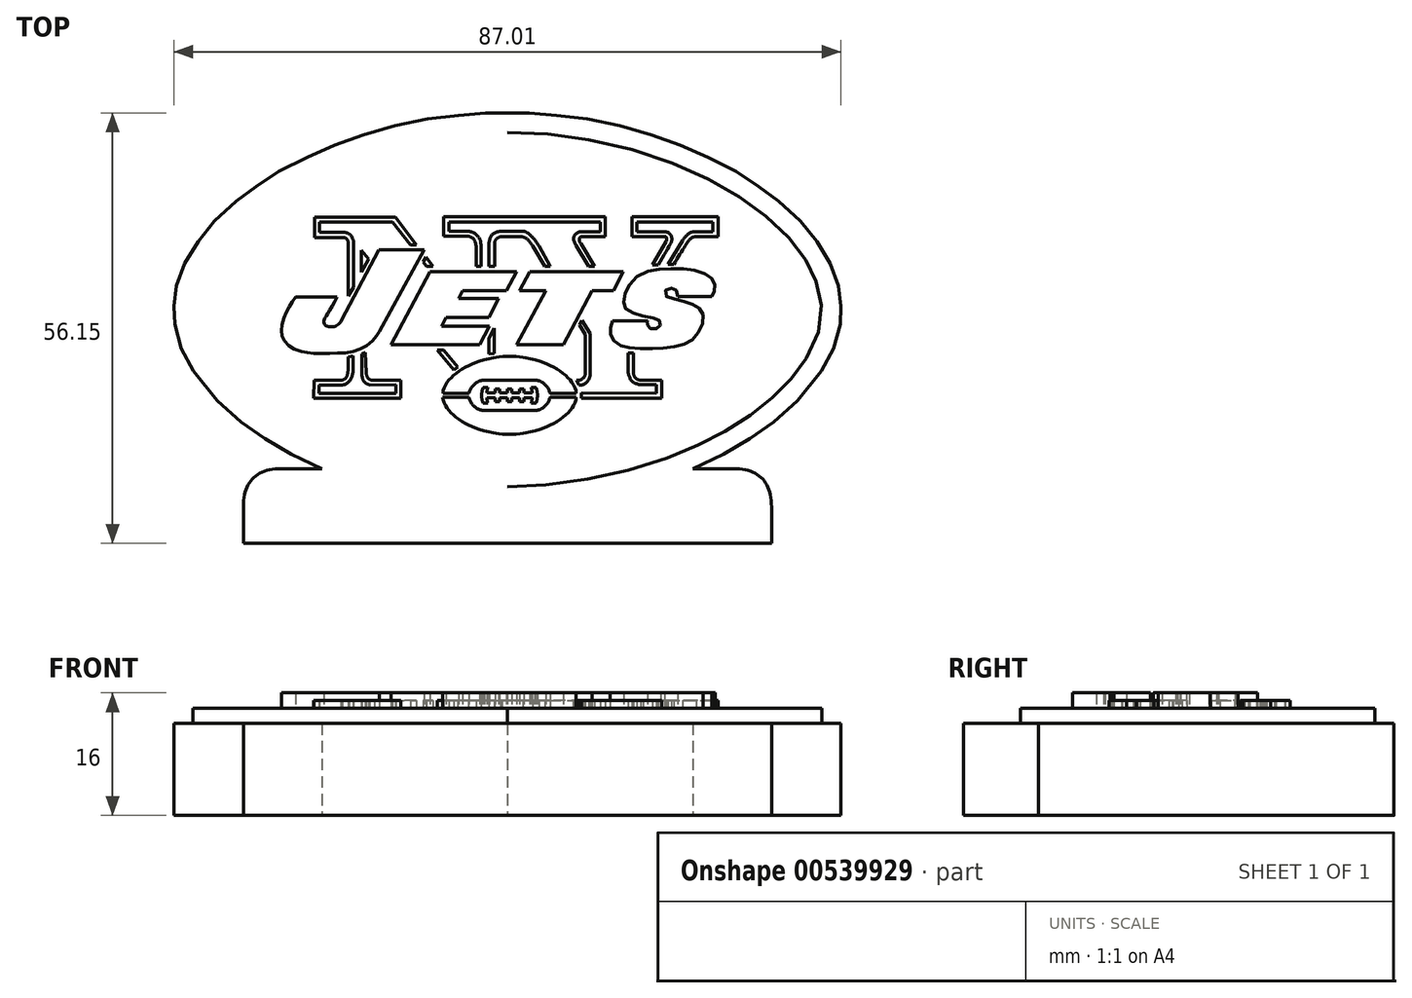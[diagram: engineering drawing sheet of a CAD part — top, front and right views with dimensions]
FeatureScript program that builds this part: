
annotation { "Feature Type Name" : "Feature", "Feature Type Description" : "" }
export const myFeature = defineFeature(function(context is Context, id is Id, definition is map)
    precondition{}
    {
        {
            var Q0;
            Q0=qCreatedBy(makeId("Top.planeOp"),FACE);
            var sketch = newSketch(context, id + "F0", { "sketchPlane" : qUnion([Q0])});
            skLineSegment(sketch, "E0", {"start": v(50, 100) * mm, "end": v(50, 0) * mm, "construction": true});
            skLineSegment(sketch, "E1", {"start": v(0, 50) * mm, "end": v(100, 50) * mm, "construction": true});
            skFitSpline(sketch, "E2", {"points": [v(50, 73.16) * mm, v(46.62, 73.07) * mm, v(44.13, 72.89) * mm, v(41.3, 72.55) * mm, v(37.34, 71.82) * mm, v(34.12, 71.04) * mm, v(31.1, 70.1) * mm, v(27.86, 68.92) * mm, v(25.45, 67.89) * mm, v(22.77, 66.55) * mm, v(20.87, 65.46) * mm, v(18.96, 64.22) * mm, v(17.3, 63.01) * mm, v(15.95, 61.91) * mm, v(14.34, 60.56) * mm, v(13.3, 59.43) * mm, v(12.35, 58.37) * mm, v(11.4, 57.02) * mm, v(10.87, 56.17) * mm, v(10.37, 55.3) * mm, v(9.9, 54.28) * mm, v(9.6, 53.32) * mm, v(9.3, 52.32) * mm, v(9.13, 51.17) * mm, v(9, 50.05) * mm, v(9.13, 48.63) * mm, v(9.42, 47.24) * mm, v(9.9, 45.89) * mm, v(10.55, 44.44) * mm, v(11.33, 43.21) * mm, v(12.02, 42.28) * mm, v(12.76, 41.3) * mm, v(13.44, 40.51) * mm, v(14.34, 39.6) * mm, v(15.47, 38.57) * mm, v(16.53, 37.65) * mm, v(17.63, 36.8) * mm, v(18.94, 35.88) * mm, v(20.3, 34.98) * mm, v(21.76, 34.1) * mm, v(23.17, 33.3) * mm, v(24.65, 32.6) * mm, v(26.26, 31.88) * mm, v(28.27, 31.03) * mm, v(30.62, 30.16) * mm, v(33.75, 29.24) * mm, v(36.82, 28.44) * mm, v(39.85, 27.86) * mm, v(43.18, 27.36) * mm, v(46.75, 27.08) * mm, v(49.83, 26.94) * mm, v(50, 26.94) * mm], "startDerivative": vector(-134.06, -2.29) * mm, "endDerivative": vector(19.01, 1.2) * mm});
            skFitSpline(sketch, "E3.MirrorCS", {"points": [v(50, 73.16) * mm, v(53.38, 73.07) * mm, v(55.87, 72.89) * mm, v(58.7, 72.55) * mm, v(62.66, 71.82) * mm, v(65.88, 71.04) * mm, v(68.9, 70.1) * mm, v(72.14, 68.92) * mm, v(74.55, 67.89) * mm, v(77.23, 66.55) * mm, v(79.13, 65.46) * mm, v(81.04, 64.22) * mm, v(82.7, 63.01) * mm, v(84.05, 61.91) * mm, v(85.66, 60.56) * mm, v(86.7, 59.43) * mm, v(87.65, 58.37) * mm, v(88.6, 57.02) * mm, v(89.13, 56.17) * mm, v(89.63, 55.3) * mm, v(90.1, 54.28) * mm, v(90.4, 53.32) * mm, v(90.7, 52.32) * mm, v(90.87, 51.17) * mm, v(91, 50.05) * mm, v(90.87, 48.63) * mm, v(90.58, 47.24) * mm, v(90.1, 45.89) * mm, v(89.45, 44.44) * mm, v(88.67, 43.21) * mm, v(87.98, 42.28) * mm, v(87.24, 41.3) * mm, v(86.56, 40.51) * mm, v(85.66, 39.6) * mm, v(84.53, 38.57) * mm, v(83.47, 37.65) * mm, v(82.37, 36.8) * mm, v(81.06, 35.88) * mm, v(79.7, 34.98) * mm, v(78.24, 34.1) * mm, v(76.83, 33.3) * mm, v(75.35, 32.6) * mm, v(73.74, 31.88) * mm, v(71.73, 31.03) * mm, v(69.38, 30.16) * mm, v(66.25, 29.24) * mm, v(63.18, 28.44) * mm, v(60.15, 27.86) * mm, v(56.82, 27.36) * mm, v(53.25, 27.08) * mm, v(50.17, 26.94) * mm, v(50, 26.94) * mm], "startDerivative": vector(134.06, -2.29) * mm, "endDerivative": vector(-19.01, 1.2) * mm});
            skSolve(sketch);
        }
        {
            var Q0;
            Q0=qCreatedBy(makeId("Top.planeOp"),FACE);
            var sketch = newSketch(context, id + "F1", { "sketchPlane" : qUnion([Q0])});
            skLineSegment(sketch, "E4", {"start": v(50, 100) * mm, "end": v(50, 2.23) * mm, "construction": true});
            skFitSpline(sketch, "E5", {"points": [v(50, 75.68) * mm, v(48.22, 75.7) * mm, v(45.68, 75.58) * mm, v(42.43, 75.28) * mm, v(38.32, 74.7) * mm, v(33.84, 73.64) * mm, v(29.88, 72.39) * mm, v(26.53, 71.15) * mm, v(23.08, 69.55) * mm, v(19.5, 67.67) * mm, v(17.21, 66.1) * mm, v(15.36, 64.76) * mm, v(12.75, 62.51) * mm, v(10.58, 60.22) * mm, v(9.15, 58.19) * mm, v(7.8, 55.82) * mm, v(6.96, 53.56) * mm, v(6.6, 52.08) * mm, v(6.5, 50.12) * mm, v(6.52, 48.8) * mm, v(6.73, 47.54) * mm, v(7.56, 44.73) * mm, v(8.64, 42.63) * mm, v(12.08, 38.23) * mm, v(15.22, 35.44) * mm, v(18, 33.43) * mm, v(21.12, 31.58) * mm, v(25.16, 29.58) * mm, v(30.48, 27.6) * mm, v(35.66, 26.1) * mm, v(39.54, 25.32) * mm, v(45.3, 24.56) * mm, v(47.72, 24.4) * mm, v(50, 24.42) * mm], "startDerivative": vector(-75.7, 2.02) * mm, "endDerivative": vector(91.69, 1.96) * mm});
            skFitSpline(sketch, "E6.MirrorCS", {"points": [v(50, 75.68) * mm, v(51.79, 75.7) * mm, v(54.32, 75.58) * mm, v(57.57, 75.28) * mm, v(61.69, 74.7) * mm, v(66.17, 73.64) * mm, v(70.13, 72.39) * mm, v(73.48, 71.15) * mm, v(76.93, 69.55) * mm, v(80.5, 67.67) * mm, v(82.8, 66.1) * mm, v(84.65, 64.76) * mm, v(87.25, 62.51) * mm, v(89.42, 60.22) * mm, v(90.86, 58.19) * mm, v(92.21, 55.82) * mm, v(93.04, 53.56) * mm, v(93.4, 52.08) * mm, v(93.5, 50.12) * mm, v(93.49, 48.8) * mm, v(93.28, 47.54) * mm, v(92.45, 44.73) * mm, v(91.37, 42.63) * mm, v(87.93, 38.23) * mm, v(84.78, 35.44) * mm, v(82, 33.43) * mm, v(78.89, 31.58) * mm, v(74.85, 29.58) * mm, v(69.53, 27.6) * mm, v(64.35, 26.1) * mm, v(60.47, 25.32) * mm, v(54.7, 24.56) * mm, v(52.28, 24.4) * mm, v(50, 24.42) * mm], "startDerivative": vector(75.7, 2.02) * mm, "endDerivative": vector(-91.69, 1.96) * mm});
            skLineSegment(sketch, "E7.bottom", {"start": v(84.45, 19.55) * mm, "end": v(15.56, 19.55) * mm});
            skLineSegment(sketch, "E7.top", {"start": v(84.45, 29.3) * mm, "end": v(15.56, 29.3) * mm});
            skLineSegment(sketch, "E7.left", {"start": v(84.45, 19.55) * mm, "end": v(84.45, 29.3) * mm});
            skLineSegment(sketch, "E7.right", {"start": v(15.56, 19.55) * mm, "end": v(15.56, 29.3) * mm});
            skSolve(sketch);
        }
        {
            var Q0;
            Q0 = qSketchRegion(id + "F1", true);
            extrude(context, id + "F2", {"entities" : qUnion([Q0]), "depth" : 12 * mm, "offsetDistance" : 25.4 * mm});
        }
        {
            var Q0;
            Q0 = qSketchRegion(id + "F0", true);
            extrude(context, id + "F3", {"entities" : qUnion([Q0]), "operationType" : NewBodyOperationType.ADD, "depth" : 14 * mm, "offsetDistance" : 25.4 * mm});
        }
        {
            var Q0;
            Q0=qCreatedBy(makeId("Top.planeOp"),FACE);
            var sketch = newSketch(context, id + "F4", { "sketchPlane" : qUnion([Q0])});
            skLineSegment(sketch, "E8", {"start": v(24.85, 62.05) * mm, "end": v(24.85, 59.47) * mm});
            skLineSegment(sketch, "E9", {"start": v(24.85, 59.47) * mm, "end": v(28.43, 59.47) * mm});
            skFitSpline(sketch, "E10", {"points": [v(28.43, 59.47) * mm, v(28.84, 59.42) * mm, v(29.08, 59.22) * mm, v(29.18, 59.04) * mm, v(29.23, 58.86) * mm, v(29.25, 58.52) * mm], "startDerivative": vector(1.8, 0.01) * mm, "endDerivative": vector(0.05, -1.65) * mm});
            skLineSegment(sketch, "E11", {"start": v(29.25, 58.52) * mm, "end": v(29.25, 51.84) * mm});
            skLineSegment(sketch, "E12", {"start": v(29.25, 51.84) * mm, "end": v(29.95, 52.98) * mm});
            skLineSegment(sketch, "E13", {"start": v(29.95, 52.98) * mm, "end": v(29.95, 58.77) * mm});
            skFitSpline(sketch, "E14", {"points": [v(29.95, 58.77) * mm, v(29.82, 59.32) * mm, v(29.41, 59.87) * mm, v(28.81, 60.12) * mm, v(28.46, 60.15) * mm], "startDerivative": vector(-0.34, 2.18) * mm, "endDerivative": vector(-1.62, -0.01) * mm});
            skLineSegment(sketch, "E15", {"start": v(28.46, 60.15) * mm, "end": v(25.49, 60.15) * mm});
            skLineSegment(sketch, "E16", {"start": v(25.49, 60.15) * mm, "end": v(25.49, 61.46) * mm});
            skLineSegment(sketch, "E17", {"start": v(25.49, 61.46) * mm, "end": v(35.03, 61.46) * mm});
            skLineSegment(sketch, "E18", {"start": v(35.03, 61.46) * mm, "end": v(37.34, 58.48) * mm});
            skLineSegment(sketch, "E19", {"start": v(37.34, 58.48) * mm, "end": v(38.12, 58.48) * mm});
            skLineSegment(sketch, "E20", {"start": v(38.12, 58.48) * mm, "end": v(35.37, 62.1) * mm});
            skLineSegment(sketch, "E21", {"start": v(35.37, 62.1) * mm, "end": v(24.85, 62.1) * mm});
            skLineSegment(sketch, "E22", {"start": v(24.85, 62.1) * mm, "end": v(24.85, 62.05) * mm});
            skLineSegment(sketch, "E23", {"start": v(30.93, 57.77) * mm, "end": v(30.93, 54.9) * mm});
            skLineSegment(sketch, "E24", {"start": v(30.93, 54.9) * mm, "end": v(31.9, 56.66) * mm});
            skLineSegment(sketch, "E25", {"start": v(31.9, 56.66) * mm, "end": v(30.93, 57.77) * mm});
            skLineSegment(sketch, "E26", {"start": v(39.37, 56.87) * mm, "end": v(40.3, 55.67) * mm});
            skLineSegment(sketch, "E27", {"start": v(40.3, 55.67) * mm, "end": v(39.45, 55.67) * mm});
            skLineSegment(sketch, "E28", {"start": v(39.45, 55.67) * mm, "end": v(39, 56.26) * mm});
            skLineSegment(sketch, "E29", {"start": v(39, 56.26) * mm, "end": v(39.37, 56.87) * mm});
            skLineSegment(sketch, "E30", {"start": v(29.33, 43.9) * mm, "end": v(29.9, 43.98) * mm});
            skLineSegment(sketch, "E31", {"start": v(29.9, 43.98) * mm, "end": v(29.9, 42.3) * mm});
            skFitSpline(sketch, "E32", {"points": [v(29.9, 42.3) * mm, v(29.81, 41.7) * mm, v(29.65, 41.15) * mm, v(29.36, 40.66) * mm, v(28.93, 40.35) * mm, v(28.7, 40.25) * mm, v(28.25, 40.21) * mm], "startDerivative": vector(-0.33, -3.22) * mm, "endDerivative": vector(-3.09, -0.14) * mm});
            skLineSegment(sketch, "E33", {"start": v(28.25, 40.21) * mm, "end": v(25.45, 40.21) * mm});
            skLineSegment(sketch, "E34", {"start": v(25.45, 40.21) * mm, "end": v(25.45, 39.1) * mm});
            skLineSegment(sketch, "E35", {"start": v(25.45, 39.1) * mm, "end": v(35.46, 39.1) * mm});
            skLineSegment(sketch, "E36", {"start": v(35.46, 39.1) * mm, "end": v(35.46, 40.25) * mm});
            skLineSegment(sketch, "E37", {"start": v(35.46, 40.25) * mm, "end": v(32.05, 40.21) * mm});
            skFitSpline(sketch, "E38", {"points": [v(32.05, 40.21) * mm, v(31.62, 40.38) * mm, v(31.27, 40.68) * mm, v(31.08, 41.12) * mm, v(30.98, 41.8) * mm], "startDerivative": vector(-1.88, 0.6) * mm, "endDerivative": vector(-0.28, 2.5) * mm});
            skLineSegment(sketch, "E39", {"start": v(30.98, 41.8) * mm, "end": v(30.98, 44.23) * mm});
            skLineSegment(sketch, "E40", {"start": v(30.98, 44.23) * mm, "end": v(31.47, 44.47) * mm});
            skLineSegment(sketch, "E41", {"start": v(31.47, 44.47) * mm, "end": v(31.56, 41.8) * mm});
            skFitSpline(sketch, "E42", {"points": [v(31.56, 41.8) * mm, v(31.64, 41.47) * mm, v(31.78, 41.15) * mm, v(32.09, 40.9) * mm, v(32.69, 40.84) * mm], "startDerivative": vector(0.33, -1.48) * mm, "endDerivative": vector(2.17, 0.04) * mm});
            skLineSegment(sketch, "E43", {"start": v(32.69, 40.84) * mm, "end": v(36.1, 40.84) * mm});
            skLineSegment(sketch, "E44", {"start": v(36.1, 40.84) * mm, "end": v(36.1, 38.49) * mm});
            skLineSegment(sketch, "E45", {"start": v(36.1, 38.49) * mm, "end": v(24.72, 38.49) * mm});
            skLineSegment(sketch, "E46", {"start": v(24.72, 38.49) * mm, "end": v(24.78, 40.84) * mm});
            skLineSegment(sketch, "E47", {"start": v(24.78, 40.84) * mm, "end": v(28.44, 40.84) * mm});
            skFitSpline(sketch, "E48", {"points": [v(28.44, 40.84) * mm, v(28.7, 40.94) * mm, v(28.98, 41.21) * mm, v(29.15, 41.67) * mm, v(29.23, 42.24) * mm], "startDerivative": vector(1.26, 0.37) * mm, "endDerivative": vector(0.2, 1.98) * mm});
            skLineSegment(sketch, "E49", {"start": v(29.23, 42.24) * mm, "end": v(29.23, 43.86) * mm});
            skLineSegment(sketch, "E50", {"start": v(29.23, 43.86) * mm, "end": v(29.33, 43.9) * mm});
            skLineSegment(sketch, "E51", {"start": v(40.87, 44.77) * mm, "end": v(41.67, 44.77) * mm});
            skLineSegment(sketch, "E52", {"start": v(41.67, 44.77) * mm, "end": v(43.5, 42.57) * mm});
            skLineSegment(sketch, "E53", {"start": v(43.5, 42.57) * mm, "end": v(43, 42.14) * mm});
            skLineSegment(sketch, "E54", {"start": v(43, 42.14) * mm, "end": v(40.87, 44.77) * mm});
            skLineSegment(sketch, "E55", {"start": v(48.29, 47.62) * mm, "end": v(48.29, 44.32) * mm});
            skLineSegment(sketch, "E56", {"start": v(48.29, 44.32) * mm, "end": v(47.56, 44.23) * mm});
            skLineSegment(sketch, "E57", {"start": v(47.56, 44.23) * mm, "end": v(47.56, 46.32) * mm});
            skLineSegment(sketch, "E58", {"start": v(47.56, 46.32) * mm, "end": v(48.29, 47.62) * mm});
            skLineSegment(sketch, "E59", {"start": v(41.76, 62.14) * mm, "end": v(62.77, 62.14) * mm});
            skLineSegment(sketch, "E60", {"start": v(62.77, 62.14) * mm, "end": v(62.77, 59.58) * mm});
            skLineSegment(sketch, "E61", {"start": v(62.77, 59.58) * mm, "end": v(59.8, 59.58) * mm});
            skFitSpline(sketch, "E62", {"points": [v(59.8, 59.58) * mm, v(59.61, 59.58) * mm, v(59.4, 59.4) * mm, v(59.39, 59.1) * mm, v(59.45, 58.85) * mm, v(59.57, 58.66) * mm], "startDerivative": vector(-1.04, 0.18) * mm, "endDerivative": vector(0.66, -0.95) * mm});
            skLineSegment(sketch, "E63", {"start": v(59.57, 58.66) * mm, "end": v(61.39, 55.71) * mm});
            skLineSegment(sketch, "E64", {"start": v(61.39, 55.71) * mm, "end": v(60.62, 55.71) * mm});
            skLineSegment(sketch, "E65", {"start": v(60.62, 55.71) * mm, "end": v(58.93, 58.43) * mm});
            skFitSpline(sketch, "E66", {"points": [v(58.93, 58.43) * mm, v(58.73, 58.9) * mm, v(58.63, 59.3) * mm, v(58.73, 59.7) * mm, v(58.93, 59.92) * mm, v(59.34, 60.15) * mm, v(59.95, 60.2) * mm], "startDerivative": vector(-1.2, 2.65) * mm, "endDerivative": vector(3.3, -0.07) * mm});
            skLineSegment(sketch, "E67", {"start": v(59.95, 60.2) * mm, "end": v(62.15, 60.2) * mm});
            skLineSegment(sketch, "E68", {"start": v(62.15, 60.2) * mm, "end": v(62.15, 61.5) * mm});
            skLineSegment(sketch, "E69", {"start": v(62.15, 61.5) * mm, "end": v(42.37, 61.5) * mm});
            skLineSegment(sketch, "E70", {"start": v(42.37, 61.5) * mm, "end": v(42.37, 60.25) * mm});
            skLineSegment(sketch, "E71", {"start": v(42.37, 60.25) * mm, "end": v(44.9, 60.25) * mm});
            skFitSpline(sketch, "E72", {"points": [v(44.9, 60.25) * mm, v(45.38, 60.15) * mm, v(45.82, 59.93) * mm, v(46.2, 59.53) * mm, v(46.4, 59.18) * mm, v(46.53, 58.67) * mm, v(46.57, 58.2) * mm], "startDerivative": vector(2.94, -0.53) * mm, "endDerivative": vector(0.11, -2.77) * mm});
            skLineSegment(sketch, "E73", {"start": v(46.57, 58.2) * mm, "end": v(46.57, 55.66) * mm});
            skLineSegment(sketch, "E74", {"start": v(46.57, 55.66) * mm, "end": v(45.98, 55.66) * mm});
            skLineSegment(sketch, "E75", {"start": v(45.98, 55.66) * mm, "end": v(45.93, 55.66) * mm});
            skLineSegment(sketch, "E76", {"start": v(45.93, 55.66) * mm, "end": v(45.93, 58.24) * mm});
            skFitSpline(sketch, "E77", {"points": [v(45.93, 58.24) * mm, v(45.8, 58.84) * mm, v(45.6, 59.24) * mm, v(45.31, 59.48) * mm, v(45.04, 59.6) * mm, v(44.52, 59.62) * mm], "startDerivative": vector(-0.4, 2.67) * mm, "endDerivative": vector(-2.63, -0.01) * mm});
            skLineSegment(sketch, "E78", {"start": v(44.52, 59.62) * mm, "end": v(41.7, 59.62) * mm});
            skLineSegment(sketch, "E79", {"start": v(41.7, 59.62) * mm, "end": v(41.7, 62.14) * mm});
            skLineSegment(sketch, "E80", {"start": v(41.7, 62.14) * mm, "end": v(41.76, 62.14) * mm});
            skLineSegment(sketch, "E81", {"start": v(47.57, 55.66) * mm, "end": v(48.35, 55.66) * mm});
            skLineSegment(sketch, "E82", {"start": v(48.35, 55.66) * mm, "end": v(48.35, 58.5) * mm});
            skLineSegment(sketch, "E83", {"start": v(47.57, 55.66) * mm, "end": v(47.57, 58.55) * mm});
            skFitSpline(sketch, "E84", {"points": [v(47.57, 58.55) * mm, v(47.68, 59.14) * mm, v(47.86, 59.65) * mm, v(48.32, 60.05) * mm, v(48.76, 60.2) * mm, v(49.07, 60.27) * mm, v(49.27, 60.28) * mm], "startDerivative": vector(0.55, 3.05) * mm, "endDerivative": vector(1.75, -0.03) * mm});
            skLineSegment(sketch, "E85", {"start": v(49.27, 60.28) * mm, "end": v(52.02, 60.28) * mm});
            skFitSpline(sketch, "E86", {"points": [v(52.02, 60.28) * mm, v(52.4, 60.17) * mm, v(52.82, 59.91) * mm, v(53.21, 59.55) * mm, v(53.62, 59.08) * mm, v(54.1, 58.36) * mm], "startDerivative": vector(2.3, -0.47) * mm, "endDerivative": vector(1.98, -3.12) * mm});
            skLineSegment(sketch, "E87", {"start": v(54.1, 58.36) * mm, "end": v(55.6, 55.67) * mm});
            skLineSegment(sketch, "E88", {"start": v(55.6, 55.67) * mm, "end": v(54.87, 55.67) * mm});
            skLineSegment(sketch, "E89", {"start": v(54.87, 55.67) * mm, "end": v(53.32, 58.36) * mm});
            skFitSpline(sketch, "E90", {"points": [v(53.32, 58.36) * mm, v(53.06, 58.7) * mm, v(52.77, 59.05) * mm, v(52.37, 59.39) * mm, v(52.1, 59.5) * mm, v(51.86, 59.57) * mm, v(51.4, 59.59) * mm], "startDerivative": vector(-1.5, 2) * mm, "endDerivative": vector(-2.75, 0) * mm});
            skLineSegment(sketch, "E91", {"start": v(51.4, 59.59) * mm, "end": v(49.1, 59.57) * mm});
            skFitSpline(sketch, "E92", {"points": [v(48.35, 58.5) * mm, v(48.35, 58.68) * mm, v(48.4, 59.03) * mm, v(48.53, 59.22) * mm, v(48.79, 59.44) * mm, v(49.1, 59.57) * mm], "startDerivative": vector(-0.02, 1.04) * mm, "endDerivative": vector(1.44, 0.46) * mm});
            skLineSegment(sketch, "E93", {"start": v(66.24, 59.58) * mm, "end": v(66.24, 62.14) * mm});
            skLineSegment(sketch, "E94", {"start": v(66.24, 62.14) * mm, "end": v(77.52, 62.14) * mm});
            skLineSegment(sketch, "E95", {"start": v(77.52, 62.14) * mm, "end": v(77.52, 59.58) * mm});
            skLineSegment(sketch, "E96", {"start": v(77.52, 59.58) * mm, "end": v(74.65, 59.58) * mm});
            skFitSpline(sketch, "E97", {"points": [v(74.65, 59.58) * mm, v(74.36, 59.54) * mm, v(73.99, 59.38) * mm, v(73.63, 59.02) * mm, v(71.69, 55.96) * mm], "startDerivative": vector(-1.91, -0.1) * mm, "endDerivative": vector(-4.67, -7.57) * mm});
            skLineSegment(sketch, "E98", {"start": v(71.69, 55.96) * mm, "end": v(70.96, 55.96) * mm});
            skLineSegment(sketch, "E99", {"start": v(70.96, 55.96) * mm, "end": v(72.84, 59.08) * mm});
            skFitSpline(sketch, "E100", {"points": [v(72.84, 59.08) * mm, v(73.16, 59.5) * mm, v(73.57, 59.88) * mm, v(74, 60.14) * mm, v(74.5, 60.2) * mm, v(75.12, 60.21) * mm], "startDerivative": vector(1.5, 2.2) * mm, "endDerivative": vector(2.99, 0.01) * mm});
            skLineSegment(sketch, "E101", {"start": v(75.12, 60.21) * mm, "end": v(76.81, 60.21) * mm});
            skLineSegment(sketch, "E102", {"start": v(76.81, 60.21) * mm, "end": v(76.81, 61.48) * mm});
            skLineSegment(sketch, "E103", {"start": v(76.81, 61.48) * mm, "end": v(66.86, 61.48) * mm});
            skLineSegment(sketch, "E104", {"start": v(66.86, 61.48) * mm, "end": v(66.86, 60.21) * mm});
            skLineSegment(sketch, "E105", {"start": v(66.86, 60.21) * mm, "end": v(70.6, 60.21) * mm});
            skFitSpline(sketch, "E106", {"points": [v(70.6, 60.21) * mm, v(70.9, 60.14) * mm, v(71.15, 59.96) * mm, v(71.36, 59.65) * mm, v(71.44, 59.35) * mm, v(71.43, 59.05) * mm, v(71.33, 58.76) * mm, v(69.68, 55.87) * mm], "startDerivative": vector(2.92, -0.46) * mm, "endDerivative": vector(-6.14, -10.46) * mm});
            skLineSegment(sketch, "E107", {"start": v(69.68, 55.87) * mm, "end": v(68.9, 55.87) * mm});
            skLineSegment(sketch, "E108", {"start": v(68.9, 55.87) * mm, "end": v(70.7, 58.9) * mm});
            skFitSpline(sketch, "E109", {"points": [v(70.7, 58.9) * mm, v(70.74, 59.07) * mm, v(70.75, 59.34) * mm, v(70.7, 59.52) * mm, v(70.49, 59.58) * mm], "startDerivative": vector(0.2, 0.65) * mm, "endDerivative": vector(-1.01, 0.12) * mm});
            skLineSegment(sketch, "E110", {"start": v(70.49, 59.58) * mm, "end": v(66.24, 59.58) * mm});
            skLineSegment(sketch, "E111", {"start": v(59.73, 48.66) * mm, "end": v(59.38, 48.05) * mm});
            skLineSegment(sketch, "E112", {"start": v(59.38, 48.05) * mm, "end": v(60.15, 46.79) * mm});
            skLineSegment(sketch, "E113", {"start": v(60.15, 46.79) * mm, "end": v(60.15, 41.83) * mm});
            skLineSegment(sketch, "E114", {"start": v(59.73, 48.66) * mm, "end": v(60.82, 46.9) * mm});
            skLineSegment(sketch, "E115", {"start": v(60.82, 46.9) * mm, "end": v(60.82, 41.67) * mm});
            skFitSpline(sketch, "E116", {"points": [v(60.15, 41.83) * mm, v(60.1, 41.4) * mm, v(59.94, 41.15) * mm, v(59.73, 40.97) * mm, v(59.54, 40.87) * mm, v(59.28, 40.86) * mm, v(59, 40.86) * mm], "startDerivative": vector(-0.08, -2.27) * mm, "endDerivative": vector(-1.73, -0.07) * mm});
            skFitSpline(sketch, "E117", {"points": [v(60.82, 41.67) * mm, v(60.7, 41.14) * mm, v(60.38, 40.62) * mm, v(59.92, 40.28) * mm, v(59.32, 40.18) * mm], "startDerivative": vector(-0.35, -2.22) * mm, "endDerivative": vector(-2.46, -0.13) * mm});
            skLineSegment(sketch, "E118", {"start": v(59, 40.86) * mm, "end": v(59.32, 40.18) * mm});
            skLineSegment(sketch, "E119", {"start": v(59.66, 39.16) * mm, "end": v(59.66, 38.5) * mm});
            skLineSegment(sketch, "E120", {"start": v(59.66, 38.5) * mm, "end": v(70.11, 38.5) * mm});
            skLineSegment(sketch, "E121", {"start": v(70.11, 38.5) * mm, "end": v(70.11, 40.83) * mm});
            skLineSegment(sketch, "E122", {"start": v(70.11, 40.83) * mm, "end": v(67.4, 40.83) * mm});
            skFitSpline(sketch, "E123", {"points": [v(67.4, 40.83) * mm, v(66.94, 40.94) * mm, v(66.6, 41.27) * mm, v(66.44, 41.7) * mm, v(66.42, 42.08) * mm], "startDerivative": vector(-1.82, 0.24) * mm, "endDerivative": vector(0.02, 1.6) * mm});
            skLineSegment(sketch, "E124", {"start": v(66.42, 42.08) * mm, "end": v(66.42, 44.4) * mm});
            skLineSegment(sketch, "E125", {"start": v(66.42, 44.4) * mm, "end": v(65.76, 44.4) * mm});
            skLineSegment(sketch, "E126", {"start": v(65.76, 44.4) * mm, "end": v(65.76, 41.76) * mm});
            skFitSpline(sketch, "E127", {"points": [v(65.76, 41.76) * mm, v(65.93, 41.22) * mm, v(66.18, 40.78) * mm, v(66.41, 40.56) * mm, v(66.78, 40.4) * mm, v(67.26, 40.25) * mm, v(67.69, 40.25) * mm], "startDerivative": vector(0.76, -2.94) * mm, "endDerivative": vector(2.59, 0.2) * mm});
            skLineSegment(sketch, "E128", {"start": v(67.69, 40.25) * mm, "end": v(69.41, 40.25) * mm});
            skLineSegment(sketch, "E129", {"start": v(69.41, 40.25) * mm, "end": v(69.41, 39.14) * mm});
            skLineSegment(sketch, "E130", {"start": v(69.41, 39.14) * mm, "end": v(59.66, 39.16) * mm});
            skSolve(sketch);
        }
        {
            var Q0;
            Q0 = qSketchRegion(id + "F4", true);
            extrude(context, id + "F5", {"entities" : qUnion([Q0]), "operationType" : NewBodyOperationType.ADD, "depth" : 15 * mm, "offsetDistance" : 25.4 * mm});
        }
        {
            var Q0;
            Q0=makeQuery(id+"F2.opExtrude","CAP_FACE",FACE,{"disambiguationData":[OSD([sQuery(id+"F1.wireOp",EDGE,"E5"),sQuery(id+"F1.wireOp",EDGE,"E6.MirrorCS")])],"isStart":false});
            var sketch = newSketch(context, id + "F6", { "sketchPlane" : qUnion([Q0])});
            skLineSegment(sketch, "E131", {"start": v(33.24, 57.86) * mm, "end": v(39.13, 57.86) * mm});
            skLineSegment(sketch, "E132", {"start": v(39.13, 57.86) * mm, "end": v(33.33, 47.2) * mm});
            skLineSegment(sketch, "E133", {"start": v(33.24, 57.86) * mm, "end": v(28.36, 48.66) * mm});
            skFitSpline(sketch, "E134", {"points": [v(28.36, 48.66) * mm, v(28.16, 48.33) * mm, v(27.82, 48.03) * mm, v(27.44, 47.82) * mm, v(26.97, 47.8) * mm, v(26.61, 47.86) * mm, v(26.3, 47.97) * mm, v(26.14, 48.15) * mm, v(26.06, 48.4) * mm, v(26.11, 48.76) * mm, v(26.35, 49.2) * mm, v(27.8, 51.67) * mm], "startDerivative": vector(-2.29, -4.22) * mm, "endDerivative": vector(7.95, 13.88) * mm});
            skLineSegment(sketch, "E135", {"start": v(27.8, 51.67) * mm, "end": v(22.5, 51.67) * mm});
            skLineSegment(sketch, "E136", {"start": v(22.5, 51.67) * mm, "end": v(22.35, 51.67) * mm});
            skFitSpline(sketch, "E137", {"points": [v(22.35, 51.67) * mm, v(22.05, 51.22) * mm, v(21.7, 50.65) * mm, v(21.36, 50.1) * mm, v(21.06, 49.47) * mm, v(20.78, 48.79) * mm, v(20.57, 47.88) * mm, v(20.56, 47.3) * mm, v(20.57, 46.78) * mm, v(20.77, 46.23) * mm, v(21.05, 45.82) * mm, v(21.63, 45.22) * mm, v(22.28, 44.89) * mm, v(23.23, 44.54) * mm, v(23.85, 44.45) * mm, v(24.63, 44.35) * mm, v(25.77, 44.3) * mm, v(26.94, 44.32) * mm, v(27.96, 44.38) * mm, v(29.08, 44.44) * mm, v(30.2, 44.67) * mm, v(31.06, 45) * mm, v(32.1, 45.66) * mm, v(32.65, 46.26) * mm, v(33.08, 46.82) * mm, v(33.33, 47.2) * mm], "startDerivative": vector(-8.97, -13.09) * mm, "endDerivative": vector(7.37, 12) * mm});
            skLineSegment(sketch, "E138", {"start": v(39.93, 55) * mm, "end": v(51.17, 55) * mm});
            skLineSegment(sketch, "E139", {"start": v(51.17, 55) * mm, "end": v(49.86, 52.54) * mm});
            skLineSegment(sketch, "E140", {"start": v(49.86, 52.54) * mm, "end": v(44.17, 52.54) * mm});
            skLineSegment(sketch, "E141", {"start": v(44.17, 52.54) * mm, "end": v(43.65, 51.5) * mm});
            skLineSegment(sketch, "E142", {"start": v(43.65, 51.5) * mm, "end": v(48.88, 51.5) * mm});
            skLineSegment(sketch, "E143", {"start": v(48.88, 51.5) * mm, "end": v(47.6, 49.02) * mm});
            skLineSegment(sketch, "E144", {"start": v(47.6, 49.02) * mm, "end": v(41.97, 49.02) * mm});
            skLineSegment(sketch, "E145", {"start": v(41.97, 49.02) * mm, "end": v(41.41, 47.87) * mm});
            skLineSegment(sketch, "E146", {"start": v(41.41, 47.87) * mm, "end": v(47.67, 47.87) * mm});
            skLineSegment(sketch, "E147", {"start": v(47.67, 47.87) * mm, "end": v(46.37, 45.45) * mm});
            skLineSegment(sketch, "E148", {"start": v(46.37, 45.45) * mm, "end": v(34.79, 45.45) * mm});
            skLineSegment(sketch, "E149", {"start": v(34.79, 45.45) * mm, "end": v(39.93, 55) * mm});
            skLineSegment(sketch, "E150", {"start": v(52.94, 55) * mm, "end": v(51.6, 52.54) * mm});
            skLineSegment(sketch, "E151", {"start": v(51.6, 52.54) * mm, "end": v(55, 52.54) * mm});
            skLineSegment(sketch, "E152", {"start": v(55, 52.54) * mm, "end": v(51.17, 45.43) * mm});
            skLineSegment(sketch, "E153", {"start": v(51.17, 45.43) * mm, "end": v(57.29, 45.43) * mm});
            skLineSegment(sketch, "E154", {"start": v(57.29, 45.43) * mm, "end": v(61.03, 52.54) * mm});
            skLineSegment(sketch, "E155", {"start": v(61.03, 52.54) * mm, "end": v(63.8, 52.54) * mm});
            skLineSegment(sketch, "E156", {"start": v(63.8, 52.54) * mm, "end": v(65.12, 55) * mm});
            skLineSegment(sketch, "E157", {"start": v(65.12, 55) * mm, "end": v(52.94, 55) * mm});
            skLineSegment(sketch, "E158", {"start": v(63.7, 48.6) * mm, "end": v(68.2, 48.6) * mm});
            skFitSpline(sketch, "E159", {"points": [v(63.7, 48.6) * mm, v(63.54, 48.19) * mm, v(63.42, 47.64) * mm, v(63.4, 47.19) * mm, v(63.48, 46.59) * mm, v(63.75, 46.15) * mm, v(64.08, 45.8) * mm, v(64.79, 45.38) * mm, v(65.31, 45.2) * mm, v(66.26, 45.02) * mm, v(67.67, 44.97) * mm, v(69.09, 44.95) * mm, v(70.22, 44.98) * mm, v(71.57, 45.15) * mm, v(72.57, 45.36) * mm, v(73.47, 45.68) * mm, v(74.23, 46.16) * mm, v(74.8, 46.86) * mm, v(75.3, 47.7) * mm, v(75.5, 48.54) * mm, v(75.49, 49.4) * mm, v(75.27, 49.95) * mm, v(74.88, 50.31) * mm, v(74.27, 50.67) * mm, v(73.65, 50.91) * mm, v(72.73, 51.19) * mm, v(71.84, 51.4) * mm, v(71.12, 51.57) * mm, v(70.65, 51.84) * mm, v(70.56, 52.36) * mm, v(70.8, 52.7) * mm, v(71.1, 52.82) * mm, v(71.5, 52.84) * mm, v(71.8, 52.76) * mm, v(72.03, 52.55) * mm, v(72.16, 52.22) * mm, v(72.2, 51.73) * mm], "startDerivative": vector(-7.94, -17.16) * mm, "endDerivative": vector(0.72, -21.94) * mm});
            skLineSegment(sketch, "E160", {"start": v(72.2, 51.73) * mm, "end": v(76.69, 51.73) * mm});
            skFitSpline(sketch, "E161", {"points": [v(76.69, 51.73) * mm, v(76.87, 52.07) * mm, v(77, 52.45) * mm, v(77.1, 52.95) * mm, v(77.03, 53.47) * mm, v(76.78, 54) * mm, v(76.23, 54.5) * mm, v(75.2, 54.97) * mm, v(73.84, 55.27) * mm, v(72.34, 55.36) * mm, v(70.52, 55.34) * mm, v(69.16, 55.21) * mm, v(67.56, 54.75) * mm, v(66.2, 53.7) * mm, v(65.72, 52.87) * mm, v(65.22, 51.82) * mm, v(65.16, 50.94) * mm, v(65.27, 50.36) * mm, v(65.65, 49.95) * mm, v(66.65, 49.5) * mm, v(67.67, 49.2) * mm, v(68.86, 48.96) * mm, v(69.59, 48.8) * mm, v(69.85, 48.56) * mm, v(69.95, 48.3) * mm, v(69.95, 47.98) * mm, v(69.7, 47.71) * mm, v(69.46, 47.55) * mm, v(69.1, 47.5) * mm, v(68.73, 47.54) * mm, v(68.5, 47.64) * mm, v(68.35, 47.87) * mm, v(68.27, 48.22) * mm, v(68.27, 48.6) * mm, v(68.2, 48.6) * mm], "startDerivative": vector(8.78, 15.15) * mm, "endDerivative": vector(-9.06, -2.9) * mm});
            skSolve(sketch);
        }
        {
            var Q0;
            Q0 = qSketchRegion(id + "F6", true);
            extrude(context, id + "F7", {"entities" : qUnion([Q0]), "operationType" : NewBodyOperationType.ADD, "depth" : 4 * mm, "offsetDistance" : 25 * mm});
        }
        {
            var Q0;
            Q0=makeQuery(id+"F2.opExtrude","CAP_FACE",FACE,{"disambiguationData":[OSD([sQuery(id+"F1.wireOp",EDGE,"E5"),sQuery(id+"F1.wireOp",EDGE,"E6.MirrorCS")])],"isStart":false});
            var sketch = newSketch(context, id + "F8", { "sketchPlane" : qUnion([Q0])});
            skLineSegment(sketch, "E162", {"start": v(41.58, 39.14) * mm, "end": v(45, 39.14) * mm});
            skLineSegment(sketch, "E163", {"start": v(50.28, 39.68) * mm, "end": v(50.28, 38) * mm, "construction": true});
            skLineSegment(sketch, "E164", {"start": v(50.28, 38) * mm, "end": v(50.28, 44.64) * mm, "construction": true});
            skLineSegment(sketch, "E165", {"start": v(50.28, 44.64) * mm, "end": v(50.28, 33.07) * mm, "construction": true});
            skFitSpline(sketch, "E166", {"points": [v(41.58, 39.14) * mm, v(41.67, 39.62) * mm, v(41.9, 40.18) * mm, v(42.3, 40.77) * mm, v(42.7, 41.2) * mm, v(43.22, 41.66) * mm, v(43.94, 42.19) * mm, v(44.81, 42.68) * mm, v(45.52, 43) * mm, v(46.66, 43.42) * mm, v(48.16, 43.76) * mm, v(48.74, 43.85) * mm, v(49.58, 43.93) * mm, v(50.28, 43.94) * mm], "startDerivative": vector(1.05, 7.87) * mm, "endDerivative": vector(9.25, -0.04) * mm});
            skFitSpline(sketch, "E167", {"points": [v(45, 39.14) * mm, v(45.03, 39.24) * mm, v(45.2, 39.7) * mm, v(45.51, 40.12) * mm, v(45.97, 40.52) * mm, v(46.28, 40.7) * mm, v(46.68, 40.82) * mm, v(47, 40.83) * mm], "startDerivative": vector(0.28, 1.05) * mm, "endDerivative": vector(2.34, -0.11) * mm});
            skLineSegment(sketch, "E168", {"start": v(47, 40.83) * mm, "end": v(50.28, 40.82) * mm});
            skLineSegment(sketch, "E169", {"start": v(50.28, 38.85) * mm, "end": v(39.27, 38.89) * mm, "construction": true});
            skLineSegment(sketch, "E170", {"start": v(39.27, 38.89) * mm, "end": v(60.53, 38.82) * mm, "construction": true});
            skLineSegment(sketch, "E171.MirrorCS", {"start": v(41.58, 38.62) * mm, "end": v(45, 38.6) * mm});
            skFitSpline(sketch, "E172.MirrorCS", {"points": [v(41.58, 38.62) * mm, v(41.67, 38.14) * mm, v(41.9, 37.58) * mm, v(42.28, 36.99) * mm, v(42.68, 36.55) * mm, v(43.2, 36.1) * mm, v(43.92, 35.56) * mm, v(44.79, 35.06) * mm, v(45.5, 34.74) * mm, v(46.63, 34.3) * mm, v(48.13, 33.96) * mm, v(48.7, 33.86) * mm, v(49.55, 33.79) * mm, v(50.25, 33.77) * mm], "startDerivative": vector(1, -7.88) * mm, "endDerivative": vector(9.25, -0.01) * mm});
            skFitSpline(sketch, "E173.MirrorCS", {"points": [v(45, 38.6) * mm, v(45.02, 38.5) * mm, v(45.2, 38.04) * mm, v(45.5, 37.61) * mm, v(45.96, 37.21) * mm, v(46.27, 37.04) * mm, v(46.67, 36.9) * mm, v(46.99, 36.9) * mm], "startDerivative": vector(0.27, -1.05) * mm, "endDerivative": vector(2.34, 0.1) * mm});
            skLineSegment(sketch, "E174.MirrorCS", {"start": v(46.99, 36.9) * mm, "end": v(50.27, 36.89) * mm});
            skFitSpline(sketch, "E175.MirrorCS", {"points": [v(58.97, 39.14) * mm, v(58.89, 39.62) * mm, v(58.65, 40.18) * mm, v(58.26, 40.77) * mm, v(57.86, 41.2) * mm, v(57.33, 41.66) * mm, v(56.62, 42.19) * mm, v(55.74, 42.68) * mm, v(55.04, 43) * mm, v(53.9, 43.42) * mm, v(52.4, 43.76) * mm, v(51.82, 43.85) * mm, v(50.98, 43.93) * mm, v(50.28, 43.94) * mm], "startDerivative": vector(-1.05, 7.87) * mm, "endDerivative": vector(-9.25, -0.04) * mm});
            skFitSpline(sketch, "E176.MirrorCS", {"points": [v(58.97, 38.62) * mm, v(58.9, 38.14) * mm, v(58.66, 37.58) * mm, v(58.27, 36.99) * mm, v(57.87, 36.55) * mm, v(57.35, 36.1) * mm, v(56.64, 35.56) * mm, v(55.77, 35.06) * mm, v(55.06, 34.74) * mm, v(53.93, 34.3) * mm, v(52.42, 33.96) * mm, v(51.85, 33.86) * mm, v(51, 33.79) * mm, v(50.3, 33.77) * mm], "startDerivative": vector(-1, -7.88) * mm, "endDerivative": vector(-9.25, -0.01) * mm});
            skFitSpline(sketch, "E177.MirrorCS", {"points": [v(55.56, 39.14) * mm, v(55.53, 39.24) * mm, v(55.35, 39.7) * mm, v(55.05, 40.12) * mm, v(54.59, 40.52) * mm, v(54.28, 40.7) * mm, v(53.87, 40.82) * mm, v(53.56, 40.83) * mm], "startDerivative": vector(-0.28, 1.05) * mm, "endDerivative": vector(-2.34, -0.11) * mm});
            skFitSpline(sketch, "E178.MirrorCS", {"points": [v(55.56, 38.6) * mm, v(55.53, 38.5) * mm, v(55.35, 38.04) * mm, v(55.05, 37.61) * mm, v(54.6, 37.21) * mm, v(54.29, 37.04) * mm, v(53.89, 36.9) * mm, v(53.57, 36.9) * mm], "startDerivative": vector(-0.27, -1.05) * mm, "endDerivative": vector(-2.34, 0.1) * mm});
            skLineSegment(sketch, "E179.MirrorCS", {"start": v(53.57, 36.9) * mm, "end": v(50.29, 36.89) * mm});
            skLineSegment(sketch, "E180.MirrorCS", {"start": v(53.56, 40.83) * mm, "end": v(50.28, 40.82) * mm});
            skLineSegment(sketch, "E181.MirrorCS", {"start": v(58.97, 39.14) * mm, "end": v(55.56, 39.14) * mm});
            skLineSegment(sketch, "E182.MirrorCS", {"start": v(58.97, 38.62) * mm, "end": v(55.56, 38.6) * mm});
            skLineSegment(sketch, "E183", {"start": v(50.25, 33.77) * mm, "end": v(50.3, 33.77) * mm});
            skLineSegment(sketch, "E184", {"start": v(50.27, 36.89) * mm, "end": v(50.29, 36.89) * mm});
            skLineSegment(sketch, "E185", {"start": v(50.23, 39.68) * mm, "end": v(50, 39.68) * mm});
            skLineSegment(sketch, "E186", {"start": v(50, 39.68) * mm, "end": v(50, 39.17) * mm});
            skLineSegment(sketch, "E187", {"start": v(50, 39.17) * mm, "end": v(48.97, 39.18) * mm});
            skLineSegment(sketch, "E188", {"start": v(48.97, 39.18) * mm, "end": v(48.97, 39.68) * mm});
            skLineSegment(sketch, "E189", {"start": v(48.97, 39.68) * mm, "end": v(48.4, 39.68) * mm});
            skLineSegment(sketch, "E190", {"start": v(48.4, 39.68) * mm, "end": v(48.4, 39.18) * mm});
            skLineSegment(sketch, "E191", {"start": v(48.4, 39.18) * mm, "end": v(47.32, 39.18) * mm});
            skFitSpline(sketch, "E192", {"points": [v(47.32, 39.18) * mm, v(47.34, 39.41) * mm, v(47.4, 39.66) * mm, v(47.46, 39.9) * mm], "startDerivative": vector(0.07, 0.71) * mm, "endDerivative": vector(0.2, 0.72) * mm});
            skLineSegment(sketch, "E193", {"start": v(47.46, 39.9) * mm, "end": v(46.84, 39.9) * mm});
            skFitSpline(sketch, "E194", {"points": [v(46.84, 39.9) * mm, v(46.75, 39.67) * mm, v(46.7, 39.46) * mm, v(46.67, 39.24) * mm, v(46.64, 38.88) * mm], "startDerivative": vector(-0.39, -0.97) * mm, "endDerivative": vector(-0.05, -1.28) * mm});
            skFitSpline(sketch, "E195.MirrorCS", {"points": [v(46.83, 37.83) * mm, v(46.75, 38.06) * mm, v(46.7, 38.27) * mm, v(46.66, 38.5) * mm, v(46.64, 38.85) * mm], "startDerivative": vector(-0.38, 0.97) * mm, "endDerivative": vector(-0.04, 1.28) * mm});
            skLineSegment(sketch, "E196.MirrorCS", {"start": v(47.45, 37.82) * mm, "end": v(46.83, 37.83) * mm});
            skFitSpline(sketch, "E197.MirrorCS", {"points": [v(47.31, 38.55) * mm, v(47.34, 38.31) * mm, v(47.39, 38.07) * mm, v(47.45, 37.82) * mm], "startDerivative": vector(0.07, -0.72) * mm, "endDerivative": vector(0.2, -0.73) * mm});
            skLineSegment(sketch, "E198.MirrorCS", {"start": v(48.4, 38.54) * mm, "end": v(47.31, 38.55) * mm});
            skLineSegment(sketch, "E199.MirrorCS", {"start": v(48.4, 38.04) * mm, "end": v(48.4, 38.54) * mm});
            skLineSegment(sketch, "E200.MirrorCS", {"start": v(48.96, 38.04) * mm, "end": v(48.4, 38.04) * mm});
            skLineSegment(sketch, "E201.MirrorCS", {"start": v(48.97, 38.54) * mm, "end": v(48.96, 38.04) * mm});
            skLineSegment(sketch, "E202.MirrorCS", {"start": v(50, 38.54) * mm, "end": v(48.97, 38.54) * mm});
            skLineSegment(sketch, "E203.MirrorCS", {"start": v(50, 38.03) * mm, "end": v(50, 38.54) * mm});
            skLineSegment(sketch, "E204.MirrorCS", {"start": v(50.22, 38.03) * mm, "end": v(50, 38.03) * mm});
            skLineSegment(sketch, "E205", {"start": v(46.64, 38.88) * mm, "end": v(46.64, 38.85) * mm});
            skFitSpline(sketch, "E206.MirrorCS", {"points": [v(53.72, 39.9) * mm, v(53.8, 39.67) * mm, v(53.85, 39.46) * mm, v(53.89, 39.24) * mm, v(53.91, 38.88) * mm], "startDerivative": vector(0.39, -0.97) * mm, "endDerivative": vector(0.05, -1.28) * mm});
            skFitSpline(sketch, "E207.MirrorCS", {"points": [v(53.72, 37.83) * mm, v(53.8, 38.06) * mm, v(53.85, 38.27) * mm, v(53.9, 38.5) * mm, v(53.91, 38.85) * mm], "startDerivative": vector(0.38, 0.97) * mm, "endDerivative": vector(0.04, 1.28) * mm});
            skLineSegment(sketch, "E208.MirrorCS", {"start": v(53.1, 37.82) * mm, "end": v(53.72, 37.83) * mm});
            skLineSegment(sketch, "E209.MirrorCS", {"start": v(53.1, 39.9) * mm, "end": v(53.72, 39.9) * mm});
            skFitSpline(sketch, "E210.MirrorCS", {"points": [v(53.24, 39.18) * mm, v(53.21, 39.41) * mm, v(53.17, 39.66) * mm, v(53.1, 39.9) * mm], "startDerivative": vector(-0.07, 0.71) * mm, "endDerivative": vector(-0.2, 0.72) * mm});
            skFitSpline(sketch, "E211.MirrorCS", {"points": [v(53.24, 38.55) * mm, v(53.22, 38.31) * mm, v(53.17, 38.07) * mm, v(53.1, 37.82) * mm], "startDerivative": vector(-0.07, -0.72) * mm, "endDerivative": vector(-0.2, -0.73) * mm});
            skLineSegment(sketch, "E212.MirrorCS", {"start": v(52.16, 38.54) * mm, "end": v(53.24, 38.55) * mm});
            skLineSegment(sketch, "E213.MirrorCS", {"start": v(52.16, 39.18) * mm, "end": v(53.24, 39.18) * mm});
            skLineSegment(sketch, "E214.MirrorCS", {"start": v(52.16, 39.68) * mm, "end": v(52.16, 39.18) * mm});
            skLineSegment(sketch, "E215.MirrorCS", {"start": v(52.16, 38.04) * mm, "end": v(52.16, 38.54) * mm});
            skLineSegment(sketch, "E216.MirrorCS", {"start": v(51.6, 38.04) * mm, "end": v(52.16, 38.04) * mm});
            skLineSegment(sketch, "E217.MirrorCS", {"start": v(51.59, 39.68) * mm, "end": v(52.16, 39.68) * mm});
            skLineSegment(sketch, "E218.MirrorCS", {"start": v(51.59, 39.18) * mm, "end": v(51.59, 39.68) * mm});
            skLineSegment(sketch, "E219.MirrorCS", {"start": v(51.6, 38.54) * mm, "end": v(51.6, 38.04) * mm});
            skLineSegment(sketch, "E220.MirrorCS", {"start": v(50.55, 38.54) * mm, "end": v(51.6, 38.54) * mm});
            skLineSegment(sketch, "E221.MirrorCS", {"start": v(50.55, 39.17) * mm, "end": v(51.59, 39.18) * mm});
            skLineSegment(sketch, "E222.MirrorCS", {"start": v(50.55, 39.68) * mm, "end": v(50.55, 39.17) * mm});
            skLineSegment(sketch, "E223.MirrorCS", {"start": v(50.56, 38.03) * mm, "end": v(50.55, 38.54) * mm});
            skLineSegment(sketch, "E224.MirrorCS", {"start": v(50.33, 39.68) * mm, "end": v(50.55, 39.68) * mm});
            skLineSegment(sketch, "E225.MirrorCS", {"start": v(50.33, 38.03) * mm, "end": v(50.56, 38.03) * mm});
            skLineSegment(sketch, "E226", {"start": v(50.33, 38.03) * mm, "end": v(50.22, 38.03) * mm});
            skLineSegment(sketch, "E227", {"start": v(50.33, 39.68) * mm, "end": v(50.23, 39.68) * mm});
            skLineSegment(sketch, "E228", {"start": v(53.91, 38.88) * mm, "end": v(53.91, 38.85) * mm});
            skSolve(sketch);
        }
        {
            var Q0;
            Q0 = qSketchRegion(id + "F8", true);
            extrude(context, id + "F9", {"entities" : qUnion([Q0]), "operationType" : NewBodyOperationType.ADD, "depth" : 4 * mm, "offsetDistance" : 25 * mm});
        }
        {
            var Q0;
            Q0=makeQuery(id+"F2.opExtrude","SWEPT_EDGE",EDGE,{"disambiguationData":[OSD([sQuery(id+"F1.wireOp",EDGE,"E7.top"),sQuery(id+"F1.wireOp",EDGE,"E7.right")])]});
            var Q1;
            Q1=makeQuery(id+"F2.opExtrude","SWEPT_EDGE",EDGE,{"disambiguationData":[OSD([sQuery(id+"F1.wireOp",EDGE,"E7.top"),sQuery(id+"F1.wireOp",EDGE,"E7.left")])]});
            fillet(context, id + "F10", {"entities" : qUnion([Q0, Q1]), "radius" : 5 * mm, "tangentPropagation" : true, "rho" : 0.5, "crossSection" : FilletCrossSection.CONIC, "allowEdgeOverflow" : false});
        }
    });
